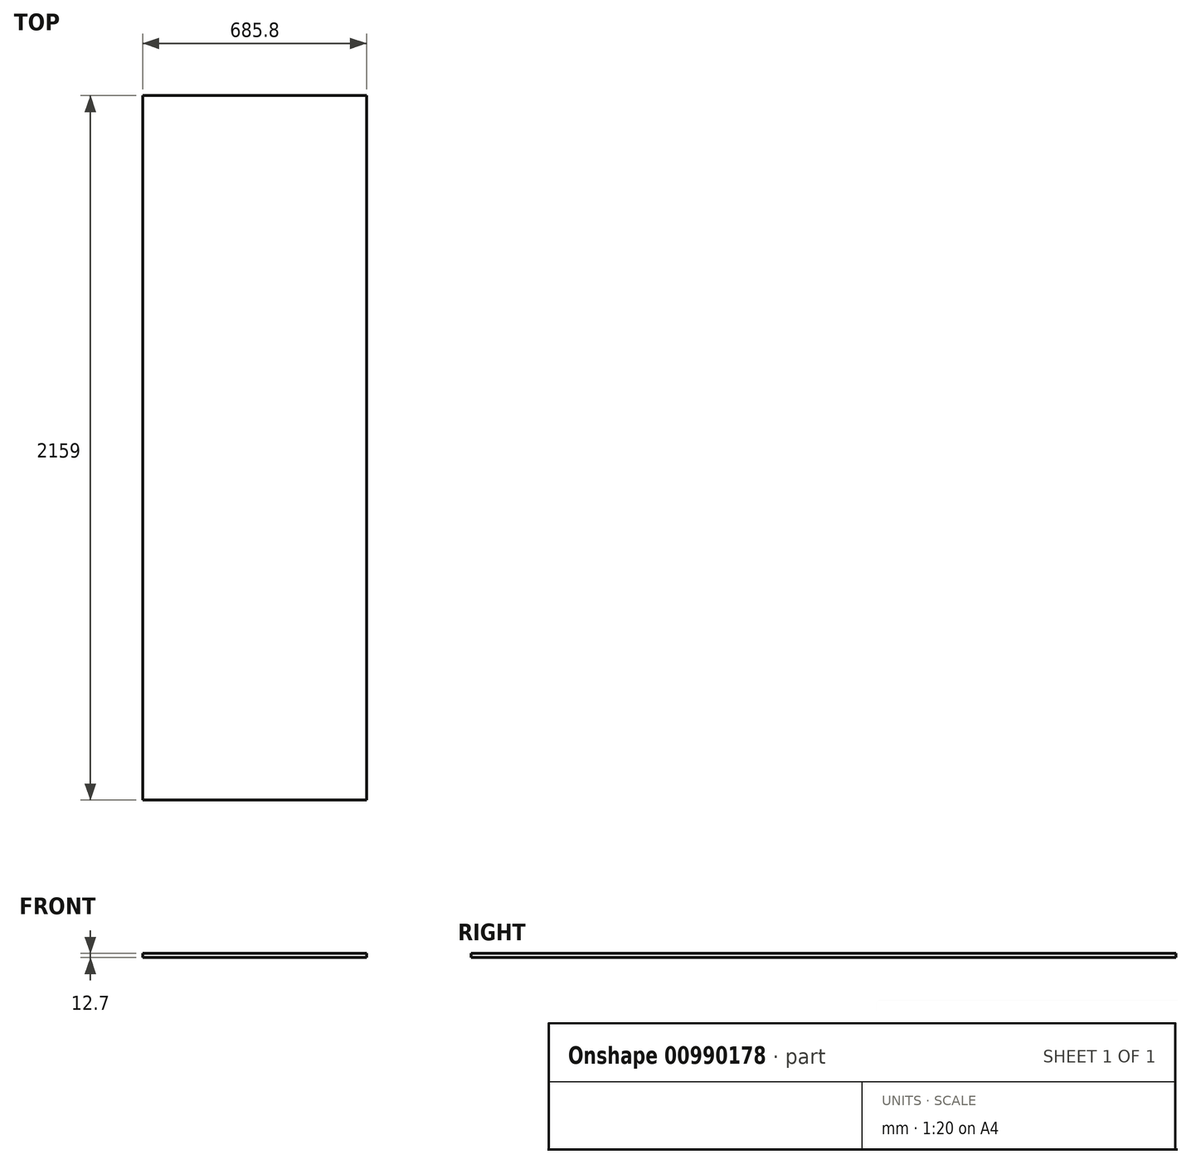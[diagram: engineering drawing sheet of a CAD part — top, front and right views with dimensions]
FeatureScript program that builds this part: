
annotation { "Feature Type Name" : "Feature", "Feature Type Description" : "" }
export const myFeature = defineFeature(function(context is Context, id is Id, definition is map)
    precondition{}
    {
        {
            var Q0;
            Q0=qCreatedBy(makeId("Top.planeOp"),FACE);
            var sketch = newSketch(context, id + "F0", { "sketchPlane" : qUnion([Q0])});
            skLineSegment(sketch, "E0.bottom", {"start": v(342.9, 1079.5) * mm, "end": v(-342.9, 1079.5) * mm});
            skLineSegment(sketch, "E0.top", {"start": v(342.9, -1079.5) * mm, "end": v(-342.9, -1079.5) * mm});
            skLineSegment(sketch, "E0.left", {"start": v(342.9, 1079.5) * mm, "end": v(342.9, -1079.5) * mm});
            skLineSegment(sketch, "E0.right", {"start": v(-342.9, 1079.5) * mm, "end": v(-342.9, -1079.5) * mm});
            skPoint(sketch, "E0.middle", {"position": v(0, 0) * mm});
            skSolve(sketch);
        }
        {
            var Q0;
            Q0=qSketchRegion(id+"F0",true);
            extrude(context, id + "F1", {"entities" : qUnion([Q0]), "depth" : 12.7 * mm, "offsetDistance" : 25.4 * mm});
        }
    });
